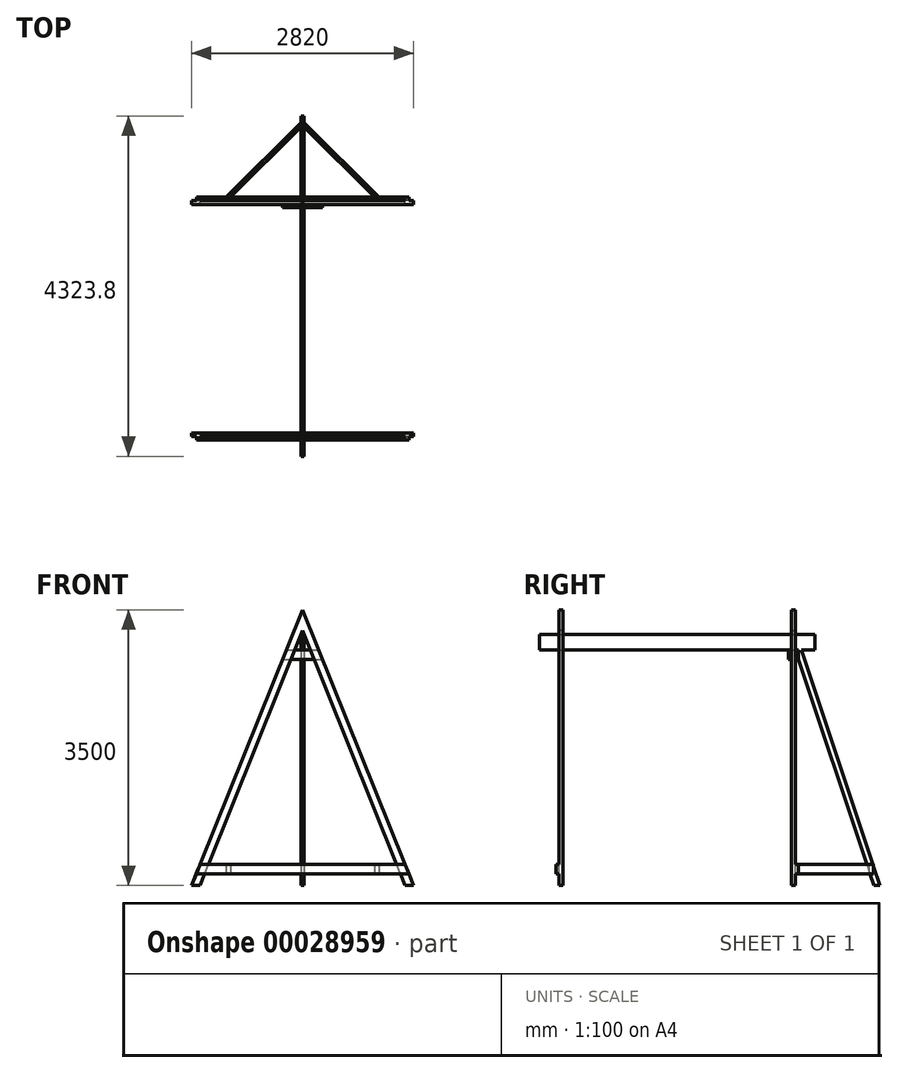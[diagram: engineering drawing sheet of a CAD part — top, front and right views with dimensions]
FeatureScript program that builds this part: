
annotation { "Feature Type Name" : "Feature", "Feature Type Description" : "" }
export const myFeature = defineFeature(function(context is Context, id is Id, definition is map)
    precondition{}
    {
        {
            var Q0;
            Q0=qCreatedBy(makeId("Front.planeOp"),FACE);
            var sketch = newSketch(context, id + "F0", { "sketchPlane" : qUnion([Q0])});
            skLineSegment(sketch, "E0", {"start": v(1410, 0) * mm, "end": v(0, 3500) * mm});
            skLineSegment(sketch, "E1.0", {"start": v(1304.35, 0) * mm, "end": v(0, 3237.74) * mm});
            skLineSegment(sketch, "E2", {"start": v(0, 3500) * mm, "end": v(0, 3237.74) * mm});
            skLineSegment(sketch, "E3", {"start": v(1410, 0) * mm, "end": v(1304.35, 0) * mm});
            skSolve(sketch);
        }
        {
            var Q0;
            Q0 = qSketchRegion(id + "F0", true);
            extrude(context, id + "F1", {"entities" : qUnion([Q0]), "depth" : 48 * mm});
        }
        {
            var Q0;
            Q0=makeQuery(id+"F1.opExtrude","SWEPT_BODY",BODY,{"disambiguationData":[OSD([sQuery(id+"F0.wireOp",EDGE,"E0"),sQuery(id+"F0.wireOp",EDGE,"E1.0"),sQuery(id+"F0.wireOp",EDGE,"E2"),sQuery(id+"F0.wireOp",EDGE,"E3")])]});
            var Q1;
            Q1=qCreatedBy(makeId("Right.planeOp"),FACE);
            mirror(context, id + "F2", {"operationType" : NewBodyOperationType.ADD, "entities" : qUnion([Q0]), "mirrorPlane" : qUnion([Q1])});
        }
        {
            var Q0;
            Q0=qCreatedBy(makeId("Front.planeOp"),FACE);
            var sketch = newSketch(context, id + "F3", { "sketchPlane" : qUnion([Q0])});
            skLineSegment(sketch, "E4.rect.bottom", {"start": v(-21, 2990.61) * mm, "end": v(21, 2990.61) * mm});
            skLineSegment(sketch, "E4.rect.top", {"start": v(-21, 3185.61) * mm, "end": v(21, 3185.61) * mm});
            skLineSegment(sketch, "E4.rect.left", {"start": v(-21, 2990.61) * mm, "end": v(-21, 3185.61) * mm});
            skLineSegment(sketch, "E4.rect.right", {"start": v(21, 2990.61) * mm, "end": v(21, 3185.61) * mm});
            skPoint(sketch, "E4.rect.middle", {"position": v(0, 3088.11) * mm});
            skSolve(sketch);
        }
        {
            var Q0;
            Q0=qCreatedBy(makeId("Front.planeOp"),FACE);
            var sketch = newSketch(context, id + "F4", { "sketchPlane" : qUnion([Q0])});
            skLineSegment(sketch, "E5", {"start": v(-205.21, 2990.61) * mm, "end": v(205.21, 2990.61) * mm});
            skLineSegment(sketch, "E6", {"start": v(-205.21, 2990.61) * mm, "end": v(-253.55, 2870.61) * mm});
            skLineSegment(sketch, "E7", {"start": v(-253.55, 2870.61) * mm, "end": v(253.55, 2870.61) * mm});
            skLineSegment(sketch, "E8", {"start": v(253.55, 2870.61) * mm, "end": v(205.21, 2990.61) * mm});
            skSolve(sketch);
        }
        {
            var Q0;
            Q0=makeQuery(id+"F4.imprint","IMPRINT",FACE,{"disambiguationData":[TD([[makeQuery(id+"F4.imprint","IMPRINT",EDGE,{"derivedFrom":sQuery(id+"F4.wireOp",EDGE,"E5")}),-1.0]])]});
            extrude(context, id + "F5", {"entities" : qUnion([Q0]), "oppositeDirection" : true, "depth" : 42 * mm});
        }
        {
            var Q0;
            Q0=qCreatedBy(makeId("Front.planeOp"),FACE);
            cPlane(context, id + "F6", {"entities" : qUnion([Q0]), "cplaneType" : CPlaneType.OFFSET, "offset" : 1500 * mm, "width" : 150 * mm, "height" : 150 * mm});
        }
        {
            var Q0;
            Q0=qCreatedBy(makeId("Front.planeOp"),FACE);
            cPlane(context, id + "F7", {"entities" : qUnion([Q0]), "cplaneType" : CPlaneType.OFFSET, "offset" : 250 * mm, "oppositeDirection" : true, "width" : 150 * mm, "height" : 150 * mm});
        }
        {
            var Q0;
            Q0=makeQuery(id+"F2.opPattern","COPY",VERTEX,{"derivedFrom":makeQuery(id+"F1.opExtrude","CAP_VERTEX",VERTEX,{"disambiguationData":[OSD([sQuery(id+"F0.wireOp",EDGE,"E0"),sQuery(id+"F0.wireOp",EDGE,"E3")])],"isStart":true}),"instanceName":"1"});
            var Q1;
            Q1=makeQuery(id+"F2.opPattern","COPY",VERTEX,{"derivedFrom":makeQuery(id+"F1.opExtrude","CAP_VERTEX",VERTEX,{"disambiguationData":[OSD([sQuery(id+"F0.wireOp",EDGE,"E0"),sQuery(id+"F0.wireOp",EDGE,"E3")])],"isStart":false}),"instanceName":"1"});
            cPlane(context, id + "F8", {"entities" : qUnion([Q0, Q1]), "cplaneType" : CPlaneType.MID_PLANE, "offset" : 150 * mm, "width" : 150 * mm, "height" : 150 * mm});
        }
        {
            var Q0;
            Q0=qCreatedBy(makeId("Front.planeOp"),FACE);
            var sketch = newSketch(context, id + "F9", { "sketchPlane" : qUnion([Q0])});
            skLineSegment(sketch, "E9", {"start": v(1349.57, 150) * mm, "end": v(-1349.57, 150) * mm});
            skLineSegment(sketch, "E10", {"start": v(-1349.57, 150) * mm, "end": v(-1301.23, 270) * mm});
            skLineSegment(sketch, "E11", {"start": v(-1301.23, 270) * mm, "end": v(1301.23, 270) * mm});
            skLineSegment(sketch, "E12", {"start": v(1301.23, 270) * mm, "end": v(1349.57, 150) * mm});
            skSolve(sketch);
        }
        {
            var Q0;
            Q0=makeQuery(id+"F9.imprint","IMPRINT",FACE,{"disambiguationData":[TD([[makeQuery(id+"F9.imprint","IMPRINT",EDGE,{"derivedFrom":sQuery(id+"F9.wireOp",EDGE,"E9")}),-1.0]])]});
            extrude(context, id + "F10", {"entities" : qUnion([Q0]), "operationType" : NewBodyOperationType.ADD, "oppositeDirection" : true, "depth" : 42 * mm});
        }
        {
            var Q0;
            Q0=qCreatedBy(makeId("Right.planeOp"),FACE);
            var sketch = newSketch(context, id + "F11", { "sketchPlane" : qUnion([Q0])});
            skLineSegment(sketch, "E13", {"start": v(42, 2870.61) * mm, "end": v(1000, 0) * mm});
            skLineSegment(sketch, "E14", {"start": v(1000, 0) * mm, "end": v(1073.8, 0) * mm});
            skLineSegment(sketch, "E15.0", {"start": v(75.75, 2990.61) * mm, "end": v(1073.8, 0) * mm});
            skLineSegment(sketch, "E16", {"start": v(75.75, 2990.61) * mm, "end": v(42, 2990.61) * mm});
            skLineSegment(sketch, "E17", {"start": v(42, 2990.61) * mm, "end": v(42, 2870.61) * mm});
            skSolve(sketch);
        }
        {
            var Q0;
            Q0=makeQuery(id+"F11.imprint","IMPRINT",FACE,{"disambiguationData":[TD([[makeQuery(id+"F11.imprint","IMPRINT",EDGE,{"derivedFrom":sQuery(id+"F11.wireOp",EDGE,"E13")}),1.0]])]});
            extrude(context, id + "F12", {"entities" : qUnion([Q0]), "endBound" : BoundingType.SYMMETRIC, "depth" : 42 * mm});
        }
        {
            var Q0;
            Q0=qCreatedBy(makeId("Top.planeOp"),FACE);
            cPlane(context, id + "F13", {"entities" : qUnion([Q0]), "cplaneType" : CPlaneType.OFFSET, "offset" : 150 * mm, "width" : 150 * mm, "height" : 150 * mm});
        }
        {
            var Q0;
            Q0=qCreatedBy(id+"F13.planeOp",FACE);
            var sketch = newSketch(context, id + "F14", { "sketchPlane" : qUnion([Q0])});
            skLineSegment(sketch, "E18", {"start": v(-911.6, 42) * mm, "end": v(-21, 932.6) * mm});
            skLineSegment(sketch, "E19", {"start": v(-21, 932.6) * mm, "end": v(-21, 992) * mm});
            skLineSegment(sketch, "E20", {"start": v(-21, 992) * mm, "end": v(-971, 42) * mm});
            skLineSegment(sketch, "E21", {"start": v(-971, 42) * mm, "end": v(-911.6, 42) * mm});
            skSolve(sketch);
        }
        {
            var Q0;
            Q0=makeQuery(id+"F14.imprint","IMPRINT",FACE,{"disambiguationData":[TD([[makeQuery(id+"F14.imprint","IMPRINT",EDGE,{"derivedFrom":sQuery(id+"F14.wireOp",EDGE,"E18")}),1.0]])]});
            var Q1;
            Q1=makeQuery(id+"F10.opExtrude","SWEPT_FACE",FACE,{"disambiguationData":[OSD([sQuery(id+"F9.wireOp",EDGE,"E11")])]});
            extrude(context, id + "F15", {"entities" : qUnion([Q0]), "endBound" : BoundingType.UP_TO_SURFACE, "endBoundEntityFace" : qUnion([Q1]), "depth" : 25 * mm});
        }
        {
            var Q0;
            Q0=makeQuery(id+"F15.opExtrude","SWEPT_BODY",BODY,{"disambiguationData":[OSD([sQuery(id+"F14.wireOp",EDGE,"E18"),sQuery(id+"F14.wireOp",EDGE,"E19"),sQuery(id+"F14.wireOp",EDGE,"E20"),sQuery(id+"F14.wireOp",EDGE,"E21")])]});
            var Q1;
            Q1=qCreatedBy(makeId("Right.planeOp"),FACE);
            mirror(context, id + "F16", {"entities" : qUnion([Q0]), "mirrorPlane" : qUnion([Q1])});
        }
        {
            var Q0;
            Q0=makeQuery(id+"F5.opExtrude","SWEPT_BODY",BODY,{"disambiguationData":[OSD([sQuery(id+"F4.wireOp",EDGE,"E5"),sQuery(id+"F4.wireOp",EDGE,"E6"),sQuery(id+"F4.wireOp",EDGE,"E7"),sQuery(id+"F4.wireOp",EDGE,"E8")])]});
            var Q1;
            Q1=qCreatedBy(id+"F8.planeOp",FACE);
            mirror(context, id + "F17", {"entities" : qUnion([Q0]), "mirrorPlane" : qUnion([Q1])});
        }
        {
            var Q0;
            Q0=makeQuery(id+"F3.imprint","IMPRINT",FACE,{"disambiguationData":[TD([[makeQuery(id+"F3.imprint","IMPRINT",EDGE,{"derivedFrom":sQuery(id+"F3.wireOp",EDGE,"E4.rect.bottom")}),1.0]])]});
            var Q1;
            Q1=qCreatedBy(id+"F6.planeOp",FACE);
            var Q2;
            Q2=qCreatedBy(id+"F7.planeOp",FACE);
            extrude(context, id + "F18", {"entities" : qUnion([Q0]), "endBound" : BoundingType.UP_TO_SURFACE, "endBoundEntityFace" : qUnion([Q1]), "depth" : 25 * mm, "hasSecondDirection" : true, "secondDirectionBound" : SecondDirectionBoundingType.UP_TO_SURFACE, "secondDirectionOppositeDirection" : true, "secondDirectionBoundEntityFace" : qUnion([Q2]), "secondDirectionDepth" : 25 * mm});
        }
        {
            var Q0;
            Q0=makeQuery(id+"F1.opExtrude","SWEPT_BODY",BODY,{"disambiguationData":[OSD([sQuery(id+"F0.wireOp",EDGE,"E0"),sQuery(id+"F0.wireOp",EDGE,"E1.0"),sQuery(id+"F0.wireOp",EDGE,"E2"),sQuery(id+"F0.wireOp",EDGE,"E3")])]});
            var Q1;
            Q1=qCreatedBy(id+"F6.planeOp",FACE);
            mirror(context, id + "F19", {"entities" : qUnion([Q0]), "mirrorPlane" : qUnion([Q1])});
        }
        {
            var Q0;
            Q0=makeQuery(id+"F18.opExtrude","SWEPT_BODY",BODY,{"disambiguationData":[OSD([sQuery(id+"F3.wireOp",EDGE,"E4.rect.bottom"),sQuery(id+"F3.wireOp",EDGE,"E4.rect.top"),sQuery(id+"F3.wireOp",EDGE,"E4.rect.left"),sQuery(id+"F3.wireOp",EDGE,"E4.rect.right")])]});
            var Q1;
            Q1=qCreatedBy(id+"F6.planeOp",FACE);
            mirror(context, id + "F20", {"operationType" : NewBodyOperationType.ADD, "entities" : qUnion([Q0]), "mirrorPlane" : qUnion([Q1])});
        }
    });
